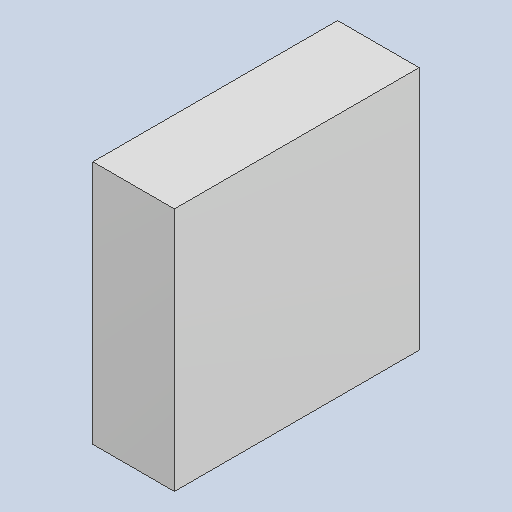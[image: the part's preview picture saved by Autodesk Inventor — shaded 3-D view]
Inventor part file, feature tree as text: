
AUTODESK INVENTOR PART (.ipt)
format: ipt  version: 2023.4 (Build 274418000, 418)  size: 81,408 bytes
history: native  units: mm
features: extrude x1
ambient origin geometry x8: Origin, YZ Plane, XZ Plane, XY Plane, X Axis, Y Axis, Z Axis, Center Point
bodies: Solid1 (feature_tree)
feature tree (1):
  extrude  "Extruded_23"  [1 undecoded]
note: 1 required parameter value undecoded (feature->parameter linkage not recoverable at this tier; creation-order binding heuristic only, values carry confidence <= 0.55)
